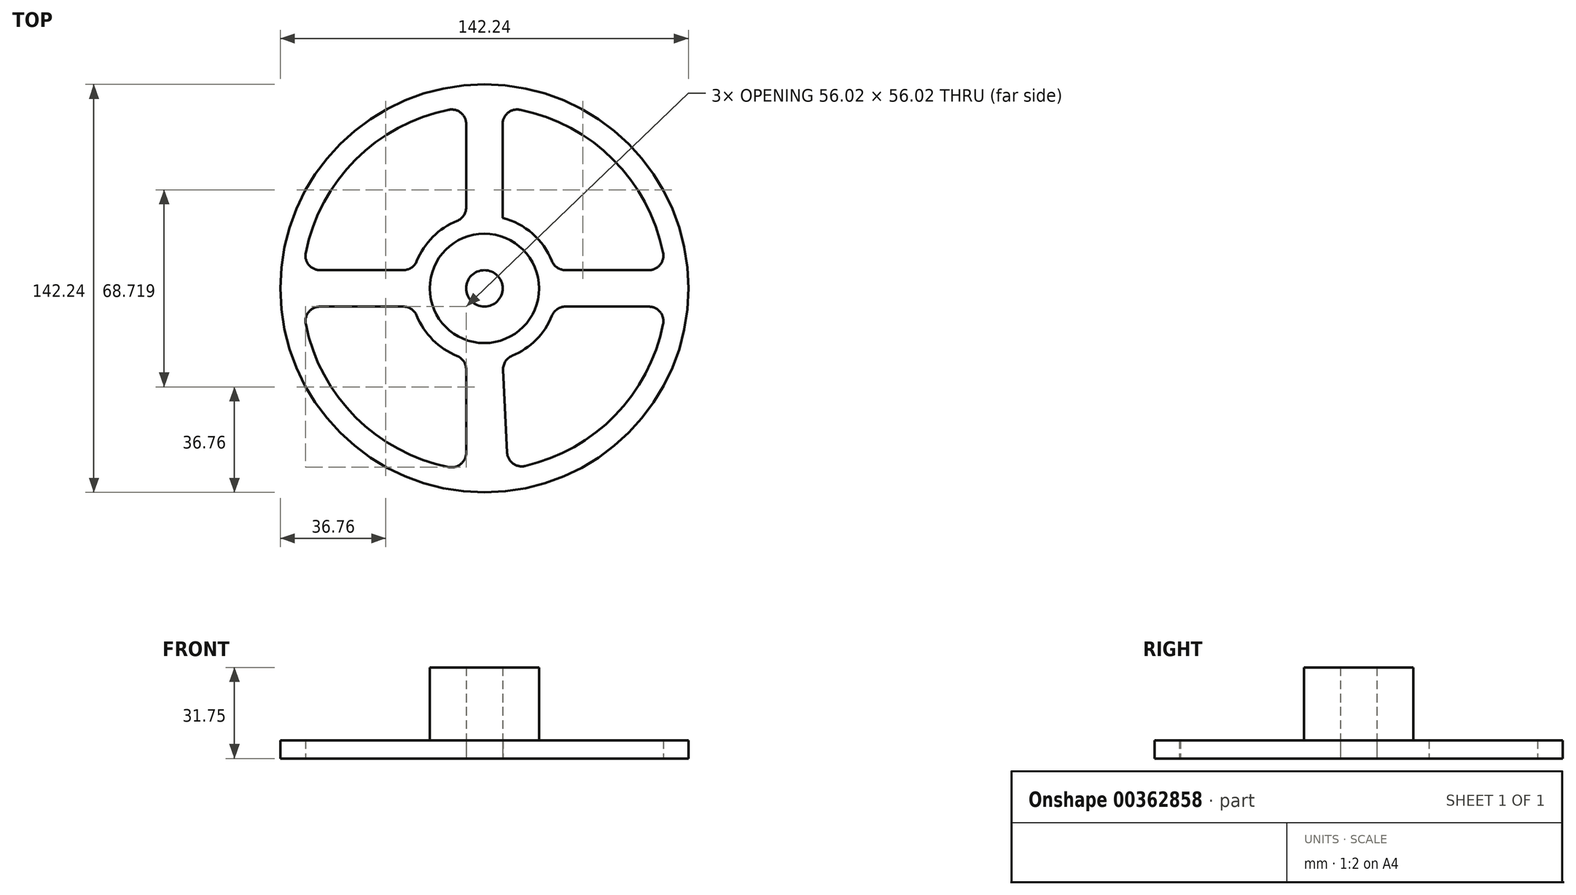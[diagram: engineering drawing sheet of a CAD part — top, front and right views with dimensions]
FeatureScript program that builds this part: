
annotation { "Feature Type Name" : "Feature", "Feature Type Description" : "" }
export const myFeature = defineFeature(function(context is Context, id is Id, definition is map)
    precondition{}
    {
        {
            var Q0;
            Q0=qCreatedBy(makeId("Top.planeOp"),FACE);
            var sketch = newSketch(context, id + "F0", { "sketchPlane" : qUnion([Q0])});
            skCircle(sketch, "E0", {"center": v(0, 0) * mm, "radius": 71.12 * mm});
            skArc(sketch, "E1", {"start": v(14.11, -61.91) * mm, "mid": v(45.5, -44.29) * mm, "end": v(62.27, -12.42) * mm});
            skArc(sketch, "E2", {"start": v(23.55, 9.53) * mm, "mid": v(16.74, 19.1) * mm, "end": v(6.35, 24.6) * mm});
            skCircle(sketch, "E3", {"center": v(0, 0) * mm, "radius": 19.05 * mm});
            skLineSegment(sketch, "E4", {"start": v(-6.35, -28.26) * mm, "end": v(-6.35, -57.3) * mm});
            skLineSegment(sketch, "E5", {"start": v(6.35, 57.3) * mm, "end": v(6.35, 24.6) * mm});
            skLineSegment(sketch, "E6", {"start": v(-28.26, 6.35) * mm, "end": v(-57.3, 6.35) * mm});
            skLineSegment(sketch, "E7", {"start": v(-57.3, -6.35) * mm, "end": v(-28.26, -6.35) * mm});
            skLineSegment(sketch, "E8", {"start": v(28.26, -6.35) * mm, "end": v(57.3, -6.35) * mm});
            skLineSegment(sketch, "E9", {"start": v(57.3, 6.35) * mm, "end": v(28.26, 6.35) * mm});
            skLineSegment(sketch, "E10.trimOffspring", {"start": v(-6.35, 28.26) * mm, "end": v(-6.35, 57.3) * mm});
            skLineSegment(sketch, "E11.trimOffspring", {"start": v(6.53, -28.43) * mm, "end": v(7.9, -57.2) * mm});
            skArc(sketch, "E12.trimOffspring", {"start": v(62.27, 12.42) * mm, "mid": v(44.9, 44.9) * mm, "end": v(12.42, 62.27) * mm});
            skArc(sketch, "E13.trimOffspring", {"start": v(-12.42, 62.27) * mm, "mid": v(-44.9, 44.9) * mm, "end": v(-62.27, 12.42) * mm});
            skArc(sketch, "E14.trimOffspring", {"start": v(-62.27, -12.42) * mm, "mid": v(-44.9, -44.9) * mm, "end": v(-12.42, -62.27) * mm});
            skPoint(sketch, "E15.visualSharp", {"position": v(8.18, -62.97) * mm});
            skArc(sketch, "E15.filletArc", {"start": v(7.9, -57.2) * mm, "mid": v(9.9, -61) * mm, "end": v(14.11, -61.91) * mm});
            skPoint(sketch, "E16.visualSharp", {"position": v(63.18, -6.35) * mm});
            skArc(sketch, "E16.filletArc", {"start": v(62.27, -12.42) * mm, "mid": v(61.22, -8.2) * mm, "end": v(57.3, -6.35) * mm});
            skArc(sketch, "E17.trimOffspring", {"start": v(-9.53, 23.55) * mm, "mid": v(-17.96, 17.96) * mm, "end": v(-23.55, 9.52) * mm});
            skArc(sketch, "E18.trimOffspring", {"start": v(-23.55, -9.53) * mm, "mid": v(-17.96, -17.96) * mm, "end": v(-9.52, -23.55) * mm});
            skArc(sketch, "E19.trimOffspring", {"start": v(9.67, -23.49) * mm, "mid": v(18.02, -17.9) * mm, "end": v(23.55, -9.52) * mm});
            skPoint(sketch, "E20.visualSharp", {"position": v(6.35, -24.6) * mm});
            skArc(sketch, "E20.filletArc", {"start": v(9.67, -23.49) * mm, "mid": v(7.32, -25.46) * mm, "end": v(6.53, -28.43) * mm});
            skPoint(sketch, "E21.visualSharp", {"position": v(24.6, -6.35) * mm});
            skArc(sketch, "E21.filletArc", {"start": v(28.26, -6.35) * mm, "mid": v(25.42, -7.22) * mm, "end": v(23.55, -9.53) * mm});
            skPoint(sketch, "E22.visualSharp", {"position": v(24.6, 6.35) * mm});
            skArc(sketch, "E22.filletArc", {"start": v(23.55, 9.53) * mm, "mid": v(25.42, 7.22) * mm, "end": v(28.26, 6.35) * mm});
            skPoint(sketch, "E23.visualSharp", {"position": v(63.18, 6.35) * mm});
            skArc(sketch, "E23.filletArc", {"start": v(57.3, 6.35) * mm, "mid": v(61.22, 8.2) * mm, "end": v(62.27, 12.42) * mm});
            skPoint(sketch, "E24.visualSharp", {"position": v(6.35, 63.18) * mm});
            skArc(sketch, "E24.filletArc", {"start": v(12.42, 62.27) * mm, "mid": v(8.2, 61.22) * mm, "end": v(6.35, 57.3) * mm});
            skPoint(sketch, "E25.visualSharp", {"position": v(-6.35, 63.18) * mm});
            skArc(sketch, "E25.filletArc", {"start": v(-6.35, 57.3) * mm, "mid": v(-8.2, 61.22) * mm, "end": v(-12.42, 62.27) * mm});
            skPoint(sketch, "E26.visualSharp", {"position": v(-63.18, 6.35) * mm});
            skArc(sketch, "E26.filletArc", {"start": v(-62.27, 12.42) * mm, "mid": v(-61.22, 8.2) * mm, "end": v(-57.3, 6.35) * mm});
            skPoint(sketch, "E27.visualSharp", {"position": v(-24.6, 6.35) * mm});
            skArc(sketch, "E27.filletArc", {"start": v(-28.26, 6.35) * mm, "mid": v(-25.42, 7.22) * mm, "end": v(-23.55, 9.52) * mm});
            skPoint(sketch, "E28.visualSharp", {"position": v(-6.35, 24.6) * mm});
            skArc(sketch, "E28.filletArc", {"start": v(-9.53, 23.55) * mm, "mid": v(-7.22, 25.42) * mm, "end": v(-6.35, 28.26) * mm});
            skPoint(sketch, "E29.visualSharp", {"position": v(-63.18, -6.35) * mm});
            skArc(sketch, "E29.filletArc", {"start": v(-57.3, -6.35) * mm, "mid": v(-61.22, -8.2) * mm, "end": v(-62.27, -12.42) * mm});
            skPoint(sketch, "E30.visualSharp", {"position": v(-24.6, -6.35) * mm});
            skArc(sketch, "E30.filletArc", {"start": v(-23.55, -9.52) * mm, "mid": v(-25.42, -7.22) * mm, "end": v(-28.26, -6.35) * mm});
            skPoint(sketch, "E31.visualSharp", {"position": v(-6.35, -24.6) * mm});
            skArc(sketch, "E31.filletArc", {"start": v(-6.35, -28.26) * mm, "mid": v(-7.22, -25.42) * mm, "end": v(-9.52, -23.55) * mm});
            skPoint(sketch, "E32.visualSharp", {"position": v(-6.35, -63.18) * mm});
            skArc(sketch, "E32.filletArc", {"start": v(-12.42, -62.27) * mm, "mid": v(-8.2, -61.22) * mm, "end": v(-6.35, -57.3) * mm});
            skSolve(sketch);
        }
        {
            var Q0;
            Q0=makeQuery(id+"F0.imprint","IMPRINT",FACE,{"disambiguationData":[TD([[makeQuery(id+"F0.imprint","IMPRINT",EDGE,{"derivedFrom":sQuery(id+"F0.wireOp",EDGE,"E0")}),1.0]])]});
            extrude(context, id + "F1", {"entities" : qUnion([Q0]), "depth" : 6.35 * mm});
        }
        {
            var Q0;
            Q0=makeQuery(id+"F0.imprint","IMPRINT",FACE,{"disambiguationData":[TD([[makeQuery(id+"F0.imprint","IMPRINT",EDGE,{"derivedFrom":sQuery(id+"F0.wireOp",EDGE,"E3")}),1.0]])]});
            extrude(context, id + "F2", {"entities" : qUnion([Q0]), "operationType" : NewBodyOperationType.ADD, "depth" : 31.75 * mm});
        }
        {
            var Q0;
            Q0=sQuery(id+"F0.wireOp",VERTEX,"E0.center");
            var Q1;
            Q1=makeQuery(id+"F1.opExtrude","SWEPT_BODY",BODY,{"disambiguationData":[OSD([sQuery(id+"F0.wireOp",EDGE,"E0"),sQuery(id+"F0.wireOp",EDGE,"E1"),sQuery(id+"F0.wireOp",EDGE,"E2"),sQuery(id+"F0.wireOp",EDGE,"E3"),sQuery(id+"F0.wireOp",EDGE,"E4"),sQuery(id+"F0.wireOp",EDGE,"E5"),sQuery(id+"F0.wireOp",EDGE,"E6"),sQuery(id+"F0.wireOp",EDGE,"E7"),sQuery(id+"F0.wireOp",EDGE,"E8"),sQuery(id+"F0.wireOp",EDGE,"E9"),sQuery(id+"F0.wireOp",EDGE,"E10.trimOffspring"),sQuery(id+"F0.wireOp",EDGE,"E11.trimOffspring"),sQuery(id+"F0.wireOp",EDGE,"E12.trimOffspring"),sQuery(id+"F0.wireOp",EDGE,"E13.trimOffspring"),sQuery(id+"F0.wireOp",EDGE,"E14.trimOffspring"),sQuery(id+"F0.wireOp",EDGE,"E15.filletArc"),sQuery(id+"F0.wireOp",EDGE,"E16.filletArc"),sQuery(id+"F0.wireOp",EDGE,"E17.trimOffspring"),sQuery(id+"F0.wireOp",EDGE,"E18.trimOffspring"),sQuery(id+"F0.wireOp",EDGE,"E19.trimOffspring"),sQuery(id+"F0.wireOp",EDGE,"E20.filletArc"),sQuery(id+"F0.wireOp",EDGE,"E21.filletArc"),sQuery(id+"F0.wireOp",EDGE,"E22.filletArc"),sQuery(id+"F0.wireOp",EDGE,"E23.filletArc"),sQuery(id+"F0.wireOp",EDGE,"E24.filletArc"),sQuery(id+"F0.wireOp",EDGE,"E25.filletArc"),sQuery(id+"F0.wireOp",EDGE,"E26.filletArc"),sQuery(id+"F0.wireOp",EDGE,"E27.filletArc"),sQuery(id+"F0.wireOp",EDGE,"E28.filletArc"),sQuery(id+"F0.wireOp",EDGE,"E29.filletArc"),sQuery(id+"F0.wireOp",EDGE,"E30.filletArc"),sQuery(id+"F0.wireOp",EDGE,"E31.filletArc"),sQuery(id+"F0.wireOp",EDGE,"E32.filletArc")])]});
            hole(context, id + "F3", {"style" : HoleStyle.SIMPLE, "endStyle" : HoleEndStyle.BLIND, "oppositeDirection" : true, "holeDiameter" : 12.7 * mm, "holeDepth" : 38.1 * mm, "tappedDepth" : 12.7 * mm, "tapClearance" : 3, "startFromSketch" : true, "locations" : qUnion([Q0]), "scope" : qUnion([Q1])});
        }
    });
